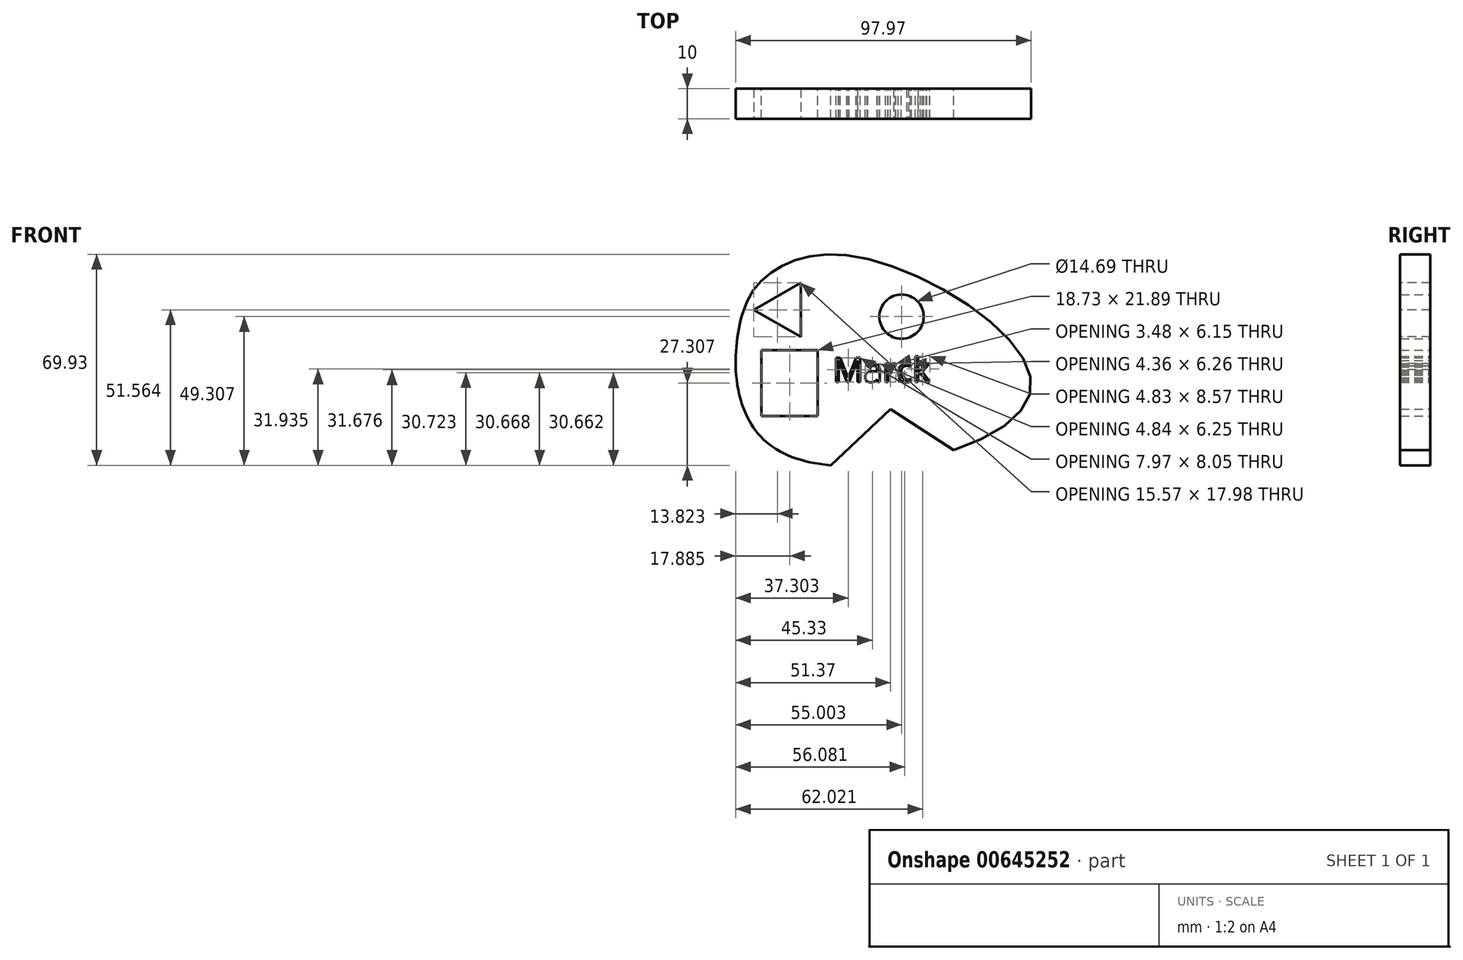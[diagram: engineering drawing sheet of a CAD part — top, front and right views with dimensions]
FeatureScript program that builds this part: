
annotation { "Feature Type Name" : "Feature", "Feature Type Description" : "" }
export const myFeature = defineFeature(function(context is Context, id is Id, definition is map)
    precondition{}
    {
        {
            var Q0;
            Q0=qCreatedBy(makeId("Front.planeOp"),FACE);
            var sketch = newSketch(context, id + "F0", { "sketchPlane" : qUnion([Q0])});
            skFitSpline(sketch, "E0", {"points": [v(-49.98, 19.97) * mm, v(-39.15, 37.57) * mm, v(-4.17, 40.95) * mm, v(46.14, -3.5) * mm, v(-35.76, -22.45) * mm, v(-49.98, 19.97) * mm]});
            skCircle(sketch, "E1", {"center": v(-28.32, 26.96) * mm, "radius": 7.72 * mm});
            skCircle(sketch, "E2", {"center": v(3.72, 22.68) * mm, "radius": 7.35 * mm});
            skText(sketch, "E3", { "text": "Marck\n", "fontName": "OpenSans-Regular.ttf"});
            skLineSegment(sketch, "E4", {"start": v(-49.1, 23.43) * mm, "end": v(-28.33, 6.43) * mm});
            skLineSegment(sketch, "E5", {"start": v(-28.33, 6.43) * mm, "end": v(-47.3, -10.85) * mm});
            skLineSegment(sketch, "E6", {"start": v(-19.76, -26.63) * mm, "end": v(0, -8.01) * mm});
            skLineSegment(sketch, "E7", {"start": v(0, -8.01) * mm, "end": v(21.02, -21.58) * mm});
            const initialGuessF0  = {"E3": [-0.01907, 0.00102, 1, 0, 0.00812]};
            skSetInitialGuess(sketch, initialGuessF0);
            skSolve(sketch);
        }
        {
            var Q0;
            {var subQ0=sQuery(id+"F0.wireOp",EDGE,"E4");Q0=makeQuery(id+"F0.imprint","IMPRINT",FACE,{"disambiguationData":[TD([[makeQuery(id+"F0.imprint","IMPRINT",EDGE,{"derivedFrom":subQ0}),-1.0]])]});}
            var Q1;
            Q1=makeQuery(id+"F0.imprint","IMPRINT",FACE,{"disambiguationData":[TD([[makeQuery(id+"F0.imprint","IMPRINT",EDGE,{"derivedFrom":sQuery(id+"F0.wireOp",EDGE,"E1")}),1.0]])]});
            var Q2;
            Q2=makeQuery(id+"F0.imprint","IMPRINT",FACE,{"disambiguationData":[TD([[makeQuery(id+"F0.imprint","IMPRINT",EDGE,{"derivedFrom":sQuery(id+"F0.wireOp",EDGE,"E1")}),-1.0]])]});
            extrude(context, id + "F1", {"entities" : qUnion([Q0, Q1, Q2]), "depth" : 10 * mm, "offsetDistance" : 25 * mm});
        }
        {
            var Q0;
            Q0=makeQuery(id+"F1.opExtrude","CAP_FACE",FACE,{"disambiguationData":[OSD([sQuery(id+"F0.wireOp",EDGE,"E0"),sQuery(id+"F0.wireOp",EDGE,"E2"),sQuery(id+"F0.wireOp",EDGE,"E3.sketch_text.stroke-0"),sQuery(id+"F0.wireOp",EDGE,"E3.sketch_text.stroke-1"),sQuery(id+"F0.wireOp",EDGE,"E3.sketch_text.stroke-2"),sQuery(id+"F0.wireOp",EDGE,"E3.sketch_text.stroke-3"),sQuery(id+"F0.wireOp",EDGE,"E3.sketch_text.stroke-4"),sQuery(id+"F0.wireOp",EDGE,"E3.sketch_text.stroke-5"),sQuery(id+"F0.wireOp",EDGE,"E3.sketch_text.stroke-6"),sQuery(id+"F0.wireOp",EDGE,"E3.sketch_text.stroke-7"),sQuery(id+"F0.wireOp",EDGE,"E3.sketch_text.stroke-8"),sQuery(id+"F0.wireOp",EDGE,"E3.sketch_text.stroke-9"),sQuery(id+"F0.wireOp",EDGE,"E3.sketch_text.stroke-10"),sQuery(id+"F0.wireOp",EDGE,"E3.sketch_text.stroke-11"),sQuery(id+"F0.wireOp",EDGE,"E3.sketch_text.stroke-12"),sQuery(id+"F0.wireOp",EDGE,"E3.sketch_text.stroke-13"),sQuery(id+"F0.wireOp",EDGE,"E3.sketch_text.stroke-14"),sQuery(id+"F0.wireOp",EDGE,"E3.sketch_text.stroke-15"),sQuery(id+"F0.wireOp",EDGE,"E3.sketch_text.stroke-16"),sQuery(id+"F0.wireOp",EDGE,"E3.sketch_text.stroke-17"),sQuery(id+"F0.wireOp",EDGE,"E3.sketch_text.stroke-18"),sQuery(id+"F0.wireOp",EDGE,"E3.sketch_text.stroke-19"),sQuery(id+"F0.wireOp",EDGE,"E3.sketch_text.stroke-20"),sQuery(id+"F0.wireOp",EDGE,"E3.sketch_text.stroke-21"),sQuery(id+"F0.wireOp",EDGE,"E3.sketch_text.stroke-22"),sQuery(id+"F0.wireOp",EDGE,"E3.sketch_text.stroke-23"),sQuery(id+"F0.wireOp",EDGE,"E3.sketch_text.stroke-24"),sQuery(id+"F0.wireOp",EDGE,"E3.sketch_text.stroke-25"),sQuery(id+"F0.wireOp",EDGE,"E3.sketch_text.stroke-26"),sQuery(id+"F0.wireOp",EDGE,"E3.sketch_text.stroke-27"),sQuery(id+"F0.wireOp",EDGE,"E3.sketch_text.stroke-28"),sQuery(id+"F0.wireOp",EDGE,"E3.sketch_text.stroke-29"),sQuery(id+"F0.wireOp",EDGE,"E3.sketch_text.stroke-30"),sQuery(id+"F0.wireOp",EDGE,"E3.sketch_text.stroke-31"),sQuery(id+"F0.wireOp",EDGE,"E3.sketch_text.stroke-32"),sQuery(id+"F0.wireOp",EDGE,"E3.sketch_text.stroke-33"),sQuery(id+"F0.wireOp",EDGE,"E3.sketch_text.stroke-34"),sQuery(id+"F0.wireOp",EDGE,"E3.sketch_text.stroke-35"),sQuery(id+"F0.wireOp",EDGE,"E3.sketch_text.stroke-36"),sQuery(id+"F0.wireOp",EDGE,"E3.sketch_text.stroke-45"),sQuery(id+"F0.wireOp",EDGE,"E3.sketch_text.stroke-46"),sQuery(id+"F0.wireOp",EDGE,"E3.sketch_text.stroke-47"),sQuery(id+"F0.wireOp",EDGE,"E3.sketch_text.stroke-48"),sQuery(id+"F0.wireOp",EDGE,"E3.sketch_text.stroke-49"),sQuery(id+"F0.wireOp",EDGE,"E3.sketch_text.stroke-50"),sQuery(id+"F0.wireOp",EDGE,"E3.sketch_text.stroke-51"),sQuery(id+"F0.wireOp",EDGE,"E3.sketch_text.stroke-52"),sQuery(id+"F0.wireOp",EDGE,"E3.sketch_text.stroke-53"),sQuery(id+"F0.wireOp",EDGE,"E3.sketch_text.stroke-54"),sQuery(id+"F0.wireOp",EDGE,"E3.sketch_text.stroke-55"),sQuery(id+"F0.wireOp",EDGE,"E3.sketch_text.stroke-56"),sQuery(id+"F0.wireOp",EDGE,"E3.sketch_text.stroke-57"),sQuery(id+"F0.wireOp",EDGE,"E3.sketch_text.stroke-58"),sQuery(id+"F0.wireOp",EDGE,"E3.sketch_text.stroke-59"),sQuery(id+"F0.wireOp",EDGE,"E3.sketch_text.stroke-60"),sQuery(id+"F0.wireOp",EDGE,"E3.sketch_text.stroke-61"),sQuery(id+"F0.wireOp",EDGE,"E3.sketch_text.stroke-62"),sQuery(id+"F0.wireOp",EDGE,"E3.sketch_text.stroke-63"),sQuery(id+"F0.wireOp",EDGE,"E3.sketch_text.stroke-64"),sQuery(id+"F0.wireOp",EDGE,"E3.sketch_text.stroke-65"),sQuery(id+"F0.wireOp",EDGE,"E3.sketch_text.stroke-66"),sQuery(id+"F0.wireOp",EDGE,"E3.sketch_text.stroke-67"),sQuery(id+"F0.wireOp",EDGE,"E3.sketch_text.stroke-68"),sQuery(id+"F0.wireOp",EDGE,"E3.sketch_text.stroke-69"),sQuery(id+"F0.wireOp",EDGE,"E3.sketch_text.stroke-70"),sQuery(id+"F0.wireOp",EDGE,"E3.sketch_text.stroke-71"),sQuery(id+"F0.wireOp",EDGE,"E3.sketch_text.stroke-72"),sQuery(id+"F0.wireOp",EDGE,"E3.sketch_text.stroke-73"),sQuery(id+"F0.wireOp",EDGE,"E3.sketch_text.stroke-74"),sQuery(id+"F0.wireOp",EDGE,"E3.sketch_text.stroke-75"),sQuery(id+"F0.wireOp",EDGE,"E3.sketch_text.stroke-76"),sQuery(id+"F0.wireOp",EDGE,"E3.sketch_text.stroke-77"),sQuery(id+"F0.wireOp",EDGE,"E3.sketch_text.stroke-78"),sQuery(id+"F0.wireOp",EDGE,"E3.sketch_text.stroke-79"),sQuery(id+"F0.wireOp",EDGE,"E3.sketch_text.stroke-80"),sQuery(id+"F0.wireOp",EDGE,"E3.sketch_text.stroke-81"),sQuery(id+"F0.wireOp",EDGE,"E3.sketch_text.stroke-82"),sQuery(id+"F0.wireOp",EDGE,"E3.sketch_text.stroke-83"),sQuery(id+"F0.wireOp",EDGE,"E3.sketch_text.stroke-84"),sQuery(id+"F0.wireOp",EDGE,"E3.sketch_text.stroke-85"),sQuery(id+"F0.wireOp",EDGE,"E3.sketch_text.stroke-86"),sQuery(id+"F0.wireOp",EDGE,"E3.sketch_text.stroke-87"),sQuery(id+"F0.wireOp",EDGE,"E6"),sQuery(id+"F0.wireOp",EDGE,"E7")])],"isStart":false});
            var sketch = newSketch(context, id + "F2", { "sketchPlane" : qUnion([Q0])});
            skCircle(sketch, "E8.cCircle", {"center": v(-34.86, 24.93) * mm, "radius": 5.19 * mm, "construction": true});
            skLineSegment(sketch, "E8.0", {"start": v(-29.67, 33.92) * mm, "end": v(-29.67, 15.94) * mm});
            skLineSegment(sketch, "E8.1", {"start": v(-29.67, 15.94) * mm, "end": v(-45.24, 24.93) * mm});
            skLineSegment(sketch, "E8.2", {"start": v(-45.24, 24.93) * mm, "end": v(-29.67, 33.92) * mm});
            skPoint(sketch, "E8.0.midPoint", {"position": v(-29.67, 24.93) * mm});
            skSolve(sketch);
        }
        {
            var Q0;
            Q0=makeQuery(id+"F2.imprint","IMPRINT",FACE,{"disambiguationData":[TD([[makeQuery(id+"F2.imprint","IMPRINT",EDGE,{"derivedFrom":sQuery(id+"F2.wireOp",EDGE,"E8.0")}),-1.0]])]});
            var Q1;
            Q1=sQuery(id+"F2.wireOp",EDGE,"E8.1");
            var Q2;
            Q2=sQuery(id+"F2.wireOp",EDGE,"E8.2");
            var Q3;
            Q3=sQuery(id+"F2.wireOp",EDGE,"E8.0");
            extrude(context, id + "F3", {"entities" : qUnion([Q0]), "operationType" : NewBodyOperationType.REMOVE, "surfaceEntities" : qUnion([Q1, Q2, Q3]), "oppositeDirection" : true, "depth" : 18.7 * mm, "offsetDistance" : 25 * mm});
        }
        {
            var Q0;
            Q0=qCreatedBy(makeId("Front.planeOp"),FACE);
            var sketch = newSketch(context, id + "F4", { "sketchPlane" : qUnion([Q0])});
            skLineSegment(sketch, "E9.bottom", {"start": v(-42.76, 11.62) * mm, "end": v(-24.03, 11.62) * mm});
            skLineSegment(sketch, "E9.top", {"start": v(-42.76, -10.27) * mm, "end": v(-24.03, -10.27) * mm});
            skLineSegment(sketch, "E9.left", {"start": v(-42.76, 11.62) * mm, "end": v(-42.76, -10.27) * mm});
            skLineSegment(sketch, "E9.right", {"start": v(-24.03, 11.62) * mm, "end": v(-24.03, -10.27) * mm});
            skSolve(sketch);
        }
        {
            var Q0;
            Q0=makeQuery(id+"F4.imprint","IMPRINT",FACE,{"disambiguationData":[TD([[makeQuery(id+"F4.imprint","IMPRINT",EDGE,{"derivedFrom":sQuery(id+"F4.wireOp",EDGE,"E9.bottom")}),-1.0]])]});
            var Q1;
            Q1=sQuery(id+"F4.wireOp",EDGE,"E9.right");
            var Q2;
            Q2=sQuery(id+"F4.wireOp",EDGE,"E9.bottom");
            var Q3;
            Q3=sQuery(id+"F4.wireOp",EDGE,"E9.left");
            var Q4;
            Q4=sQuery(id+"F4.wireOp",EDGE,"E9.top");
            extrude(context, id + "F5", {"entities" : qUnion([Q0]), "operationType" : NewBodyOperationType.REMOVE, "surfaceEntities" : qUnion([Q1, Q2, Q3, Q4]), "depth" : 17 * mm, "offsetDistance" : 25 * mm});
        }
    });
